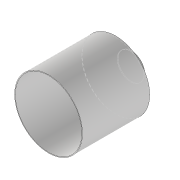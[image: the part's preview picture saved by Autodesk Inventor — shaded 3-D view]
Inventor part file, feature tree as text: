
AUTODESK INVENTOR PART (.ipt)
format: ipt  version: 2020 (Build 240168000, 168)  size: 145,408 bytes
history: native  units: mm
features: sketch x4, extrude x2, revolve x1, plane x1
ambient origin geometry x8: Origin, YZ Plane, XZ Plane, XY Plane, X Axis, Y Axis, Z Axis, Center Point
bodies: Volumenkörper1 (feature_tree)
feature tree (8):
  revolve  "Umdrehung1"
  sketch  "Skizze3"  dims[d2=5.0mm d3=500.0mm]
  plane  "Arbeitsebene1"
  extrude  "Extrusion2"  Depth=5.0mm
  extrude  "Extrusion3"  Depth=500.0mm
  sketch  "Skizze1"  dims[d0=5.0mm d1=5.0mm]
  sketch  "Skizze4"  dims[d4=500.0mm]
  sketch  "Skizze5"  dims[d5=500.0mm d6=200.0mm d7=90.0deg d12=180.0mm d13=105.0mm d14=10.0mm d15=0.0mm d16=170.0mm d17=0.0mm d18=0.0mm]
